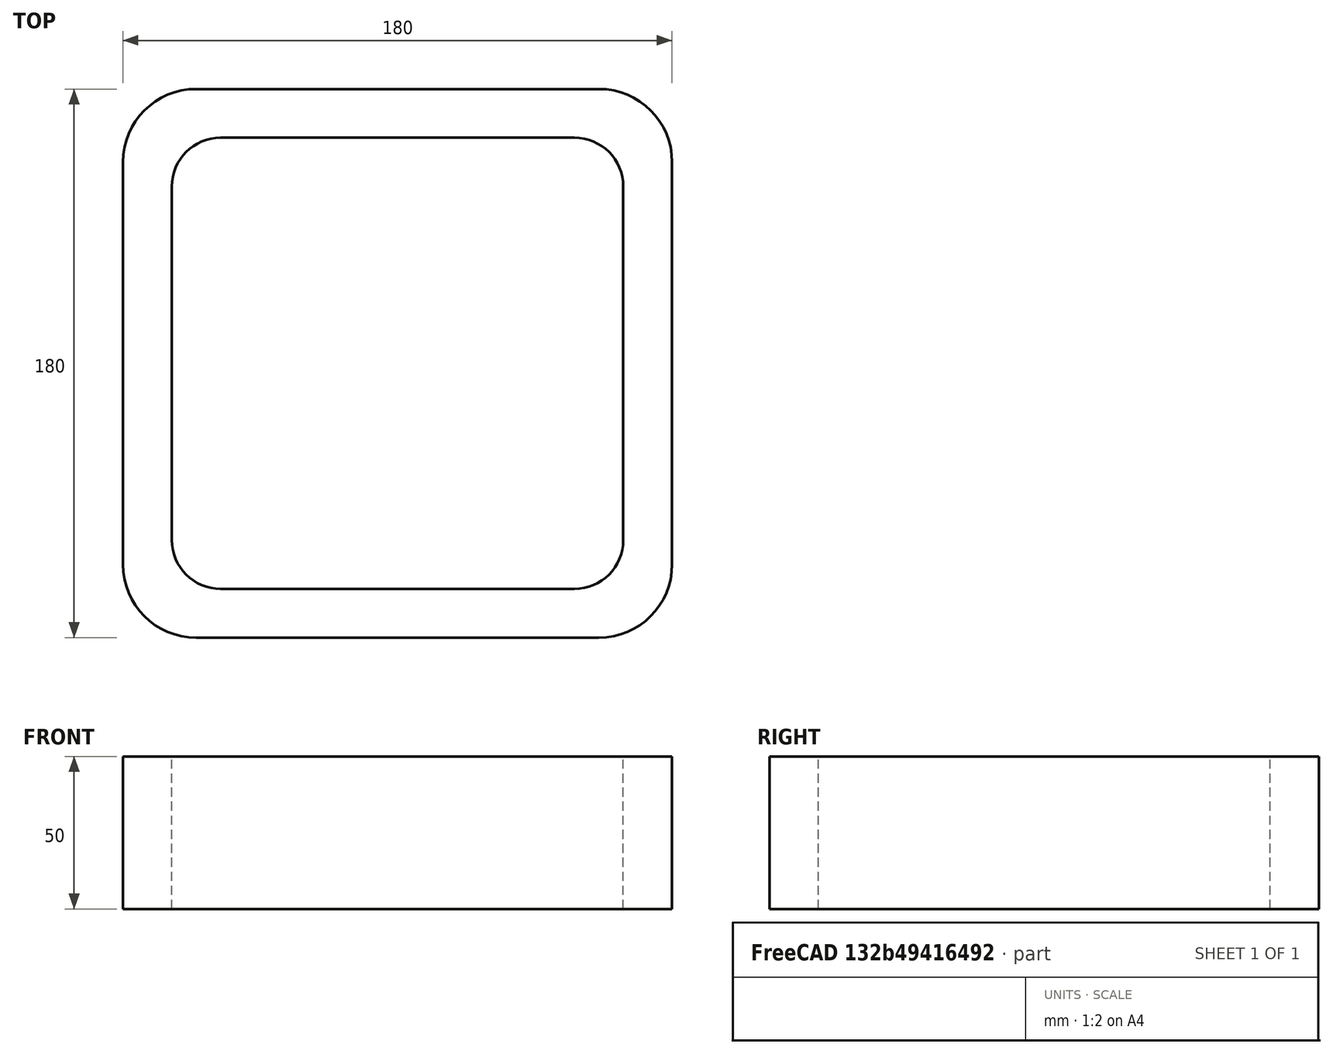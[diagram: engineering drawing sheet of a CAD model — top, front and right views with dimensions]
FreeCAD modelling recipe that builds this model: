
FCSTD DOCUMENT  (FreeCAD 0.15R4671 (Git))
Label: Square hollow section 180x180x16 EN10219 S235JRH
License: All rights reserved
LicenseURL: http://en.wikipedia.org/wiki/All_rights_reserved
objects: Sketcher::SketchObject×1, Part::Extrusion×1
note: 2 computed .brp shape members not serialized (recipe doc carries the construction recipe); baked Part::Feature solids carry a one-line shape summary decoded from their .brp

FEATURE [Sketcher::SketchObject] Sketch
  sketch-geometry (16):
    g0: LineSegment StartX=-58 StartY=74 StartZ=0 EndX=58 EndY=74 EndZ=0
    g1: LineSegment StartX=74 StartY=58 StartZ=0 EndX=74 EndY=-58 EndZ=0
    g2: LineSegment StartX=58 StartY=-74 StartZ=0 EndX=-58 EndY=-74 EndZ=0
    g3: LineSegment StartX=-74 StartY=-58 StartZ=0 EndX=-74 EndY=58 EndZ=0
    g4: LineSegment StartX=-66 StartY=90 StartZ=0 EndX=66 EndY=90 EndZ=0
    g5: LineSegment StartX=90 StartY=66 StartZ=0 EndX=90 EndY=-66 EndZ=0
    g6: LineSegment StartX=66 StartY=-90 StartZ=0 EndX=-66 EndY=-90 EndZ=0
    g7: LineSegment StartX=-90 StartY=-66 StartZ=0 EndX=-90 EndY=66 EndZ=0
    g8: ArcOfCircle CenterX=-58 CenterY=58 CenterZ=0 NormalX=0 NormalY=0 NormalZ=1 Radius=16 StartAngle=1.5708 EndAngle=3.14159
    g9: ArcOfCircle CenterX=58 CenterY=58 CenterZ=0 NormalX=0 NormalY=0 NormalZ=1 Radius=16 StartAngle=0 EndAngle=1.5708
    g10: ArcOfCircle CenterX=58 CenterY=-58 CenterZ=0 NormalX=0 NormalY=0 NormalZ=1 Radius=16 StartAngle=4.71239 EndAngle=6.28319
    g11: ArcOfCircle CenterX=-58 CenterY=-58 CenterZ=0 NormalX=0 NormalY=0 NormalZ=1 Radius=16 StartAngle=3.14159 EndAngle=4.71239
    g12: ArcOfCircle CenterX=66 CenterY=66 CenterZ=0 NormalX=0 NormalY=0 NormalZ=1 Radius=24 StartAngle=0 EndAngle=1.5708
    g13: ArcOfCircle CenterX=66 CenterY=-66 CenterZ=0 NormalX=0 NormalY=0 NormalZ=1 Radius=24 StartAngle=4.71239 EndAngle=6.28319
    g14: ArcOfCircle CenterX=-66 CenterY=-66 CenterZ=0 NormalX=0 NormalY=0 NormalZ=1 Radius=24 StartAngle=3.14159 EndAngle=4.71239
    g15: ArcOfCircle CenterX=-66 CenterY=66 CenterZ=0 NormalX=0 NormalY=0 NormalZ=1 Radius=24 StartAngle=1.5708 EndAngle=3.14159
  constraints (36):
    c: Horizontal(g2)
    c: Vertical(g3)
    c: Horizontal(g6)
    c: Vertical(g7)
    c: Tangent(g3,g8) = 1.5708
    c: Tangent(g0,g8) = 1.5708
    c: Tangent(g0,g9) = 1.5708
    c: Tangent(g1,g9) = 1.5708
    c: Tangent(g1,g10) = 1.5708
    c: Tangent(g2,g10) = 1.5708
    c: Tangent(g2,g11) = 1.5708
    c: Tangent(g3,g11) = 1.5708
    c: Tangent(g4,g12) = 1.5708
    c: Tangent(g5,g12) = 1.5708
    c: Tangent(g5,g13) = 1.5708
    c: Tangent(g6,g13) = 1.5708
    c: Tangent(g6,g14) = 1.5708
    c: Tangent(g7,g14) = 1.5708
    c: Tangent(g7,g15) = 1.5708
    c: Tangent(g4,g15) = 1.5708
    c: Equal(g9,g8)
    c: Equal(g9,g11)
    c: Equal(g9,g10)
    c: Equal(g12,g15)
    c: Equal(g12,g14)
    c: Equal(g12,g13)
    c: Symmetric(g4,g6,g-1)
    c: Symmetric(g7,g5,g-2)
    c: DistanceY(g4,g6) = -180
    c: DistanceX(g7,g5) = 180
    c: Symmetric(g3,g1,g-2)
    c: Symmetric(g0,g2,g-1)
    c: DistanceY(g0,g4) = 16
    c: DistanceX(g5,g1) = -16
    c: Radius(g9) = 16
    c: Radius(g12) = 24
FEATURE [Part::Extrusion] Extrude  label="Square hollow section 180x180x16 EN10219 S235JRH"
  Base = -> Sketch
  Dir = (0,0,50)
  Solid = true
